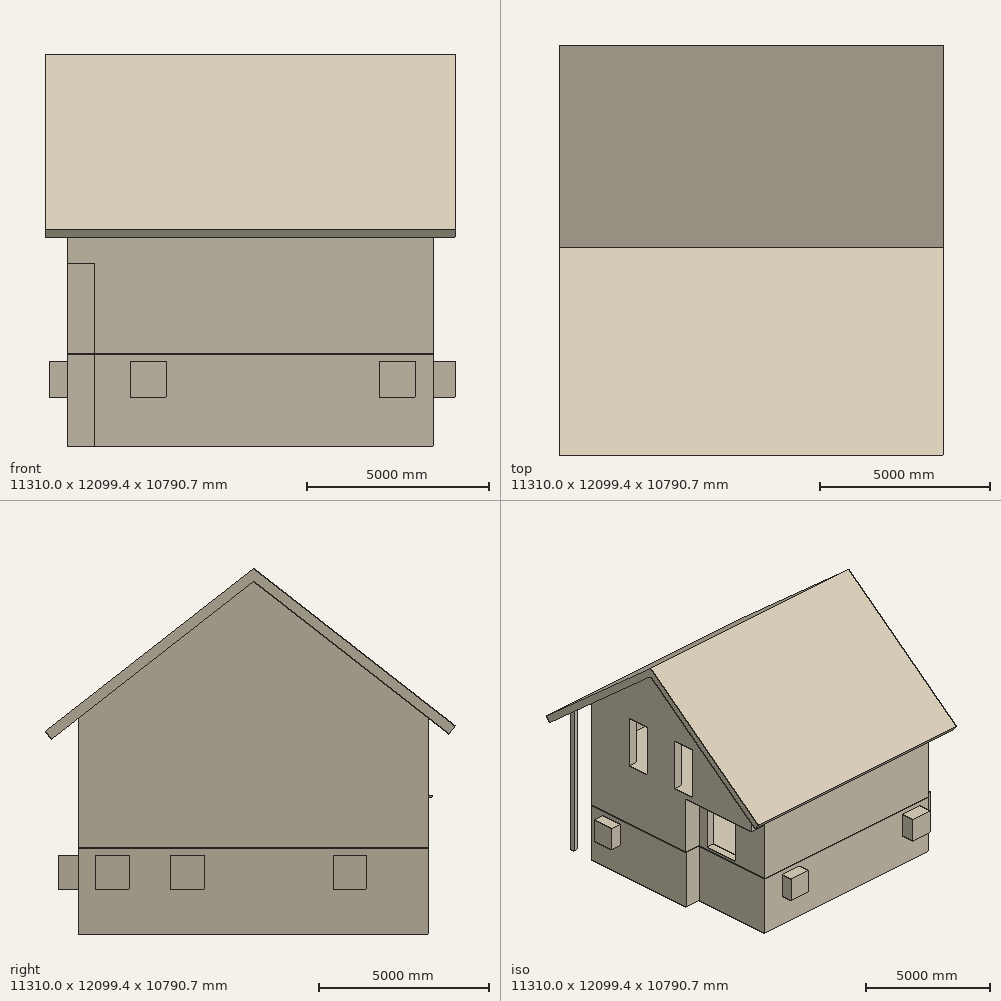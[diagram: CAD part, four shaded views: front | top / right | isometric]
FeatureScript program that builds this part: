
annotation { "Feature Type Name" : "Feature", "Feature Type Description" : "" }
export const myFeature = defineFeature(function(context is Context, id is Id, definition is map)
    precondition{}
    {
        {
            var Q0;
            Q0=qCreatedBy(makeId("Top.planeOp"),FACE);
            var sketch = newSketch(context, id + "F0", { "sketchPlane" : qUnion([Q0])});
            skLineSegment(sketch, "E0", {"start": v(0, 3573.84) * mm, "end": v(0, -3596.64) * mm, "construction": true});
            skLineSegment(sketch, "E1", {"start": v(-3920.01, 0) * mm, "end": v(4005.74, 0) * mm, "construction": true});
            skLineSegment(sketch, "E2.bottom", {"start": v(-435, 5165) * mm, "end": v(5055, 5165) * mm});
            skLineSegment(sketch, "E2.top", {"start": v(-4305, -5165) * mm, "end": v(5055, -5165) * mm});
            skLineSegment(sketch, "E2.left", {"start": v(-5055, 3965) * mm, "end": v(-5055, -1415) * mm});
            skLineSegment(sketch, "E2.right", {"start": v(5055, 5165) * mm, "end": v(5055, -5165) * mm});
            skPoint(sketch, "E2.middle", {"position": v(0, 0) * mm});
            skLineSegment(sketch, "E3", {"start": v(-5055, -1415) * mm, "end": v(-4305, -1415) * mm});
            skLineSegment(sketch, "E4", {"start": v(-4305, -1415) * mm, "end": v(-4305, -5165) * mm});
            skLineSegment(sketch, "E5", {"start": v(-435, 5165) * mm, "end": v(-435, 3965) * mm});
            skLineSegment(sketch, "E6", {"start": v(-435, 3965) * mm, "end": v(-5055, 3965) * mm});
            skLineSegment(sketch, "E7.bottom", {"start": v(-5055, 5165) * mm, "end": v(-4855, 5165) * mm});
            skLineSegment(sketch, "E7.top", {"start": v(-5055, 4965) * mm, "end": v(-4855, 4965) * mm});
            skLineSegment(sketch, "E7.left", {"start": v(-5055, 5165) * mm, "end": v(-5055, 4965) * mm});
            skLineSegment(sketch, "E7.right", {"start": v(-4855, 5165) * mm, "end": v(-4855, 4965) * mm});
            skSolve(sketch);
        }
        {
            var Q0;
            Q0=makeQuery(id+"F0.imprint","IMPRINT",FACE,{"disambiguationData":[TD([[makeQuery(id+"F0.imprint","IMPRINT",EDGE,{"derivedFrom":sQuery(id+"F0.wireOp",EDGE,"E2.bottom")}),-1.0]])]});
            var Q1;
            Q1=makeQuery(id+"F0.imprint","IMPRINT",FACE,{"disambiguationData":[TD([[makeQuery(id+"F0.imprint","IMPRINT",EDGE,{"derivedFrom":sQuery(id+"F0.wireOp",EDGE,"E7.bottom")}),-1.0]])]});
            extrude(context, id + "F1", {"entities" : qUnion([Q0, Q1]), "depth" : 7880 * mm});
        }
        {
            var Q0;
            Q0=makeQuery(id+"F0.imprint","IMPRINT",FACE,{"disambiguationData":[TD([[makeQuery(id+"F0.imprint","IMPRINT",EDGE,{"derivedFrom":sQuery(id+"F0.wireOp",EDGE,"E2.bottom")}),-1.0]])]});
            var Q1;
            Q1=makeQuery(id+"F0.imprint","IMPRINT",FACE,{"disambiguationData":[TD([[makeQuery(id+"F0.imprint","IMPRINT",EDGE,{"derivedFrom":sQuery(id+"F0.wireOp",EDGE,"E7.bottom")}),-1.0]])]});
            extrude(context, id + "F2", {"entities" : qUnion([Q0, Q1]), "operationType" : NewBodyOperationType.ADD, "oppositeDirection" : true, "depth" : 2530 * mm});
        }
        {
            var Q0;
            Q0=makeQuery(id+"F1.opExtrude","CAP_FACE",FACE,{"disambiguationData":[OSD([sQuery(id+"F0.wireOp",EDGE,"E2.bottom"),sQuery(id+"F0.wireOp",EDGE,"E2.top"),sQuery(id+"F0.wireOp",EDGE,"E2.left"),sQuery(id+"F0.wireOp",EDGE,"E2.right")])],"isStart":false});
            shell(context, id + "F3", {"entities" : qUnion([Q0]), "thickness" : 360 * mm});
        }
        {
            var Q0;
            {var subQ0=sQuery(id+"F0.wireOp",EDGE,"E2.right");Q0=makeQuery(id+"F2.boolean.opBoolean","MERGE",FACE,{"derivedFrom":[makeQuery(id+"F1.opExtrude","SWEPT_FACE",FACE,{"disambiguationData":[OSD([subQ0])]}),makeQuery(id+"F2.opExtrude","SWEPT_FACE",FACE,{"disambiguationData":[OSD([subQ0])]})]});}
            var sketch = newSketch(context, id + "F4", { "sketchPlane" : qUnion([Q0])});
            skLineSegment(sketch, "E8", {"start": v(0, 10151.05) * mm, "end": v(0, -3326.69) * mm, "construction": true});
            skPoint(sketch, "E9", {"position": v(0, 7880) * mm});
            skLineSegment(sketch, "E10", {"start": v(0, 7880) * mm, "end": v(5165, 3844.66) * mm});
            skLineSegment(sketch, "E11", {"start": v(0, 7880) * mm, "end": v(-5165, 3844.66) * mm});
            skLineSegment(sketch, "E12", {"start": v(5165, 3844.66) * mm, "end": v(5165, 7880) * mm});
            skLineSegment(sketch, "E13", {"start": v(5165, 7880) * mm, "end": v(0, 7880) * mm});
            skLineSegment(sketch, "E14", {"start": v(0, 7880) * mm, "end": v(-5165, 7880) * mm});
            skLineSegment(sketch, "E15", {"start": v(-5165, 7880) * mm, "end": v(-5165, 3844.66) * mm});
            skSolve(sketch);
        }
        {
            var Q0;
            Q0 = qSketchRegion(id + "F4", true);
            var Q1;
            {var subQ0=sQuery(id+"F0.wireOp",EDGE,"E2.left");Q1=makeQuery(id+"F2.boolean.opBoolean","MERGE",FACE,{"derivedFrom":[makeQuery(id+"F1.opExtrude","SWEPT_FACE",FACE,{"disambiguationData":[OSD([subQ0])]}),makeQuery(id+"F2.opExtrude","SWEPT_FACE",FACE,{"disambiguationData":[OSD([subQ0])]})]});}
            extrude(context, id + "F5", {"entities" : qUnion([Q0]), "operationType" : NewBodyOperationType.REMOVE, "endBound" : BoundingType.UP_TO_SURFACE, "oppositeDirection" : true, "endBoundEntityFace" : qUnion([Q1]), "depth" : 25 * mm});
        }
        {
            var Q0;
            Q0=qCreatedBy(makeId("Right.planeOp"),FACE);
            var sketch = newSketch(context, id + "F6", { "sketchPlane" : qUnion([Q0])});
            skLineSegment(sketch, "E16", {"start": v(0, 7880) * mm, "end": v(5765, 3375.89) * mm});
            skLineSegment(sketch, "E17", {"start": v(0, 7880) * mm, "end": v(-5965, 3219.63) * mm});
            skLineSegment(sketch, "E18.0", {"start": v(0, 8260.7) * mm, "end": v(-6149.7, 3456.03) * mm});
            skLineSegment(sketch, "E18.1", {"start": v(0, 8260.7) * mm, "end": v(5949.7, 3612.3) * mm});
            skLineSegment(sketch, "E19", {"start": v(5949.7, 3612.3) * mm, "end": v(5765, 3375.89) * mm});
            skLineSegment(sketch, "E20", {"start": v(-6149.7, 3456.03) * mm, "end": v(-5965, 3219.63) * mm});
            skSolve(sketch);
        }
        {
            var Q0;
            Q0 = qSketchRegion(id + "F6", true);
            extrude(context, id + "F7", {"entities" : qUnion([Q0]), "operationType" : NewBodyOperationType.ADD, "depth" : 5655 * mm, "hasSecondDirection" : true, "secondDirectionOppositeDirection" : true, "secondDirectionDepth" : 5655 * mm});
        }
        {
            var Q0;
            Q0=qCreatedBy(makeId("Top.planeOp"),FACE);
            cPlane(context, id + "F8", {"entities" : qUnion([Q0]), "cplaneType" : CPlaneType.OFFSET, "offset" : 2500 * mm, "width" : 150 * mm, "height" : 150 * mm});
        }
        {
            var Q0;
            Q0=qCreatedBy(id+"F8.planeOp",FACE);
            var sketch = newSketch(context, id + "F9", { "sketchPlane" : qUnion([Q0])});
            skLineSegment(sketch, "E21.bottom", {"start": v(-4305, -1415) * mm, "end": v(-5055, -1415) * mm});
            skLineSegment(sketch, "E21.top", {"start": v(-4305, -5165) * mm, "end": v(-5055, -5165) * mm});
            skLineSegment(sketch, "E21.left", {"start": v(-4305, -1415) * mm, "end": v(-4305, -5165) * mm});
            skLineSegment(sketch, "E21.right", {"start": v(-5055, -1415) * mm, "end": v(-5055, -5165) * mm});
            skSolve(sketch);
        }
        {
            var Q0;
            Q0 = qSketchRegion(id + "F9", true);
            extrude(context, id + "F10", {"entities" : qUnion([Q0]), "operationType" : NewBodyOperationType.ADD, "endBound" : BoundingType.UP_TO_NEXT, "depth" : 25 * mm});
        }
        {
            var Q0;
            Q0=qCreatedBy(makeId("Top.planeOp"),FACE);
            cPlane(context, id + "F11", {"entities" : qUnion([Q0]), "cplaneType" : CPlaneType.OFFSET, "offset" : 200 * mm, "oppositeDirection" : true, "width" : 150 * mm, "height" : 150 * mm});
        }
        {
            var Q0;
            Q0=qCreatedBy(id+"F11.planeOp",FACE);
            var sketch = newSketch(context, id + "F12", { "sketchPlane" : qUnion([Q0])});
            skLineSegment(sketch, "E22.bottom", {"start": v(-5055, 3335) * mm, "end": v(-5555, 3335) * mm});
            skLineSegment(sketch, "E22.top", {"start": v(-5055, 2335) * mm, "end": v(-5555, 2335) * mm});
            skLineSegment(sketch, "E22.left", {"start": v(-5055, 3335) * mm, "end": v(-5055, 2335) * mm});
            skLineSegment(sketch, "E22.right", {"start": v(-5555, 3335) * mm, "end": v(-5555, 2335) * mm});
            skLineSegment(sketch, "E23.bottom", {"start": v(5055, 3335) * mm, "end": v(5555, 3335) * mm});
            skLineSegment(sketch, "E23.top", {"start": v(5055, 2335) * mm, "end": v(5555, 2335) * mm});
            skLineSegment(sketch, "E23.left", {"start": v(5055, 3335) * mm, "end": v(5055, 2335) * mm});
            skLineSegment(sketch, "E23.right", {"start": v(5555, 3335) * mm, "end": v(5555, 2335) * mm});
            skLineSegment(sketch, "E24.bottom", {"start": v(5055, -1465) * mm, "end": v(5555, -1465) * mm});
            skLineSegment(sketch, "E24.top", {"start": v(5055, -2465) * mm, "end": v(5555, -2465) * mm});
            skLineSegment(sketch, "E24.left", {"start": v(5055, -1465) * mm, "end": v(5055, -2465) * mm});
            skLineSegment(sketch, "E24.right", {"start": v(5555, -1465) * mm, "end": v(5555, -2465) * mm});
            skLineSegment(sketch, "E25.bottom", {"start": v(5055, -3665) * mm, "end": v(5655, -3665) * mm});
            skLineSegment(sketch, "E25.top", {"start": v(5055, -4665) * mm, "end": v(5655, -4665) * mm});
            skLineSegment(sketch, "E25.left", {"start": v(5055, -3665) * mm, "end": v(5055, -4665) * mm});
            skLineSegment(sketch, "E25.right", {"start": v(5655, -3665) * mm, "end": v(5655, -4665) * mm});
            skLineSegment(sketch, "E26.bottom", {"start": v(4555, -5165) * mm, "end": v(3555, -5165) * mm});
            skLineSegment(sketch, "E26.top", {"start": v(4555, -5765) * mm, "end": v(3555, -5765) * mm});
            skLineSegment(sketch, "E26.left", {"start": v(4555, -5165) * mm, "end": v(4555, -5765) * mm});
            skLineSegment(sketch, "E26.right", {"start": v(3555, -5165) * mm, "end": v(3555, -5765) * mm});
            skLineSegment(sketch, "E27.bottom", {"start": v(-3305, -5165) * mm, "end": v(-2305, -5165) * mm});
            skLineSegment(sketch, "E27.top", {"start": v(-3305, -5665) * mm, "end": v(-2305, -5665) * mm});
            skLineSegment(sketch, "E27.left", {"start": v(-3305, -5165) * mm, "end": v(-3305, -5665) * mm});
            skLineSegment(sketch, "E27.right", {"start": v(-2305, -5165) * mm, "end": v(-2305, -5665) * mm});
            skSolve(sketch);
        }
        {
            var Q0;
            Q0 = qSketchRegion(id + "F12", true);
            extrude(context, id + "F13", {"entities" : qUnion([Q0]), "operationType" : NewBodyOperationType.ADD, "oppositeDirection" : true, "depth" : 1000 * mm});
        }
        {
            var Q0;
            {var subQ0=sQuery(id+"F0.wireOp",EDGE,"E4");Q0=makeQuery(id+"F2.boolean.opBoolean","MERGE",FACE,{"derivedFrom":[makeQuery(id+"F1.opExtrude","SWEPT_FACE",FACE,{"disambiguationData":[OSD([subQ0])]}),makeQuery(id+"F2.opExtrude","SWEPT_FACE",FACE,{"disambiguationData":[OSD([subQ0])]})]});}
            var sketch = newSketch(context, id + "F14", { "sketchPlane" : qUnion([Q0])});
            skLineSegment(sketch, "E28", {"start": v(-4224.63, 0) * mm, "end": v(4783.34, 0) * mm, "construction": true});
            skLineSegment(sketch, "E29.bottom", {"start": v(1869.6, 2250) * mm, "end": v(3469.6, 2250) * mm});
            skLineSegment(sketch, "E29.top", {"start": v(1869.6, 150) * mm, "end": v(3469.6, 150) * mm});
            skLineSegment(sketch, "E29.left", {"start": v(1869.6, 2250) * mm, "end": v(1869.6, 150) * mm});
            skLineSegment(sketch, "E29.right", {"start": v(3469.6, 2250) * mm, "end": v(3469.6, 150) * mm});
            skSolve(sketch);
        }
        {
            var Q0;
            Q0 = qSketchRegion(id + "F14", true);
            extrude(context, id + "F15", {"entities" : qUnion([Q0]), "operationType" : NewBodyOperationType.REMOVE, "endBound" : BoundingType.UP_TO_NEXT, "oppositeDirection" : true, "depth" : 25 * mm});
        }
        {
            var Q0;
            Q0=qCreatedBy(makeId("Top.planeOp"),FACE);
            var sketch = newSketch(context, id + "F16", { "sketchPlane" : qUnion([Q0])});
            skLineSegment(sketch, "E30", {"start": v(-5055, 3965) * mm, "end": v(-434.34, 3965) * mm});
            skLineSegment(sketch, "E31", {"start": v(-434.34, 3965) * mm, "end": v(-434.34, 5165) * mm});
            skLineSegment(sketch, "E32", {"start": v(-434.34, 5165) * mm, "end": v(5055, 5165) * mm});
            skLineSegment(sketch, "E33", {"start": v(5055, 5165) * mm, "end": v(5055, -5165) * mm});
            skLineSegment(sketch, "E34", {"start": v(5055, -5165) * mm, "end": v(-4305, -5165) * mm});
            skLineSegment(sketch, "E35", {"start": v(-4305, -5165) * mm, "end": v(-4305, -1415) * mm});
            skLineSegment(sketch, "E36", {"start": v(-4305, -1415) * mm, "end": v(-5055, -1415) * mm});
            skLineSegment(sketch, "E37", {"start": v(-5055, -1415) * mm, "end": v(-5055, 3965) * mm});
            skLineSegment(sketch, "E38.0", {"start": v(-5045, -1405) * mm, "end": v(-5045, 3955) * mm});
            skLineSegment(sketch, "E38.1", {"start": v(-4295, -1405) * mm, "end": v(-5045, -1405) * mm});
            skLineSegment(sketch, "E38.2", {"start": v(-5045, 3955) * mm, "end": v(-424.34, 3955) * mm});
            skLineSegment(sketch, "E38.3", {"start": v(-4295, -5155) * mm, "end": v(-4295, -1405) * mm});
            skLineSegment(sketch, "E38.4", {"start": v(-424.34, 3955) * mm, "end": v(-424.34, 5155) * mm});
            skLineSegment(sketch, "E38.5", {"start": v(-424.34, 5155) * mm, "end": v(5045, 5155) * mm});
            skLineSegment(sketch, "E38.6", {"start": v(5045, 5155) * mm, "end": v(5045, -5155) * mm});
            skLineSegment(sketch, "E38.7", {"start": v(5045, -5155) * mm, "end": v(-4295, -5155) * mm});
            skSolve(sketch);
        }
        {
            var Q0;
            Q0 = qSketchRegion(id + "F16", true);
            extrude(context, id + "F17", {"entities" : qUnion([Q0]), "operationType" : NewBodyOperationType.REMOVE, "depth" : 25 * mm});
        }
        {
            var Q0;
            {var subQ0=sQuery(id+"F0.wireOp",EDGE,"E2.bottom");Q0=makeQuery(id+"F2.boolean.opBoolean","MERGE",FACE,{"derivedFrom":[makeQuery(id+"F1.opExtrude","SWEPT_FACE",FACE,{"disambiguationData":[OSD([subQ0])]}),makeQuery(id+"F2.opExtrude","SWEPT_FACE",FACE,{"disambiguationData":[OSD([subQ0])]})]});}
            var sketch = newSketch(context, id + "F18", { "sketchPlane" : qUnion([Q0])});
            skCircle(sketch, "E39", {"center": v(-1365, 1530.35) * mm, "radius": 25 * mm});
            skSolve(sketch);
        }
        {
            var Q0;
            Q0 = qSketchRegion(id + "F18", true);
            extrude(context, id + "F19", {"entities" : qUnion([Q0]), "operationType" : NewBodyOperationType.ADD, "depth" : 100 * mm});
        }
        {
            var Q0;
            {var subQ3=sQuery(id+"F0.wireOp",EDGE,"E2.top");var subQ4=sQuery(id+"F9.wireOp",EDGE,"E21.right");var subQ5=sQuery(id+"F0.wireOp",EDGE,"E2.left");Q0=makeQuery(id+"F17.boolean.opBoolean","SPLIT",FACE,{"disambiguationData":[TD([makeQuery(id+"F1.opExtrude","SWEPT_FACE",FACE,{"disambiguationData":[OSD([subQ3])]})])],"derivedFrom":makeQuery(id+"F10.boolean.opBoolean","MERGE",FACE,{"derivedFrom":[makeQuery(id+"F2.boolean.opBoolean","MERGE",FACE,{"derivedFrom":[makeQuery(id+"F1.opExtrude","SWEPT_FACE",FACE,{"disambiguationData":[OSD([subQ5])]}),makeQuery(id+"F2.opExtrude","SWEPT_FACE",FACE,{"disambiguationData":[OSD([subQ5])]})]}),makeQuery(id+"F10.opExtrude","SWEPT_FACE",FACE,{"disambiguationData":[OSD([subQ4])]})]})});}
            var sketch = newSketch(context, id + "F20", { "sketchPlane" : qUnion([Q0])});
            skLineSegment(sketch, "E40.bottom", {"start": v(5165, 2500) * mm, "end": v(-3965, 2500) * mm});
            skLineSegment(sketch, "E40.top", {"start": v(5165, 2740) * mm, "end": v(-3965, 2740) * mm});
            skLineSegment(sketch, "E40.left", {"start": v(5165, 2500) * mm, "end": v(5165, 2740) * mm});
            skLineSegment(sketch, "E40.right", {"start": v(-3965, 2500) * mm, "end": v(-3965, 2740) * mm});
            skLineSegment(sketch, "E41", {"start": v(-2751.87, 5730) * mm, "end": v(2751.87, 5730) * mm});
            skLineSegment(sketch, "E42", {"start": v(2751.87, 5730) * mm, "end": v(3059.06, 5490) * mm});
            skLineSegment(sketch, "E43", {"start": v(3059.06, 5490) * mm, "end": v(-3059.06, 5490) * mm});
            skLineSegment(sketch, "E44", {"start": v(-3059.06, 5490) * mm, "end": v(-2751.87, 5730) * mm});
            skSolve(sketch);
        }
        {
            var Q0;
            Q0 = qSketchRegion(id + "F20", true);
            var Q1;
            {var subQ2=sQuery(id+"F0.wireOp",EDGE,"E2.right");Q1=makeQuery(id+"F17.boolean.opBoolean","SPLIT",FACE,{"disambiguationData":[TD([makeQuery(id+"F7.opExtrude","SWEPT_FACE",FACE,{"disambiguationData":[OSD([sQuery(id+"F6.wireOp",EDGE,"E16")])]})])],"derivedFrom":makeQuery(id+"F2.boolean.opBoolean","MERGE",FACE,{"derivedFrom":[makeQuery(id+"F1.opExtrude","SWEPT_FACE",FACE,{"disambiguationData":[OSD([subQ2])]}),makeQuery(id+"F2.opExtrude","SWEPT_FACE",FACE,{"disambiguationData":[OSD([subQ2])]})]})});}
            extrude(context, id + "F21", {"entities" : qUnion([Q0]), "operationType" : NewBodyOperationType.ADD, "endBound" : BoundingType.UP_TO_SURFACE, "oppositeDirection" : true, "endBoundEntityFace" : qUnion([Q1]), "depth" : 25 * mm});
        }
        {
            var Q0;
            {var subQ3=sQuery(id+"F0.wireOp",EDGE,"E2.top");var subQ4=sQuery(id+"F9.wireOp",EDGE,"E21.right");var subQ5=sQuery(id+"F0.wireOp",EDGE,"E2.left");Q0=makeQuery(id+"F17.boolean.opBoolean","SPLIT",FACE,{"disambiguationData":[TD([makeQuery(id+"F1.opExtrude","SWEPT_FACE",FACE,{"disambiguationData":[OSD([subQ3])]})])],"derivedFrom":makeQuery(id+"F10.boolean.opBoolean","MERGE",FACE,{"derivedFrom":[makeQuery(id+"F2.boolean.opBoolean","MERGE",FACE,{"derivedFrom":[makeQuery(id+"F1.opExtrude","SWEPT_FACE",FACE,{"disambiguationData":[OSD([subQ5])]}),makeQuery(id+"F2.opExtrude","SWEPT_FACE",FACE,{"disambiguationData":[OSD([subQ5])]})]}),makeQuery(id+"F10.opExtrude","SWEPT_FACE",FACE,{"disambiguationData":[OSD([subQ4])]})]})});}
            var sketch = newSketch(context, id + "F22", { "sketchPlane" : qUnion([Q0])});
            skLineSegment(sketch, "E45.bottom", {"start": v(-1792.5, 2740) * mm, "end": v(-782.5, 2740) * mm});
            skLineSegment(sketch, "E45.top", {"start": v(-1792.5, 4940) * mm, "end": v(-782.5, 4940) * mm});
            skLineSegment(sketch, "E45.left", {"start": v(-1792.5, 2740) * mm, "end": v(-1792.5, 4940) * mm});
            skLineSegment(sketch, "E45.right", {"start": v(-782.5, 2740) * mm, "end": v(-782.5, 4940) * mm});
            skLineSegment(sketch, "E46.bottom", {"start": v(782.5, 2740) * mm, "end": v(1792.5, 2740) * mm});
            skLineSegment(sketch, "E46.top", {"start": v(782.5, 4940) * mm, "end": v(1792.5, 4940) * mm});
            skLineSegment(sketch, "E46.left", {"start": v(782.5, 2740) * mm, "end": v(782.5, 4940) * mm});
            skLineSegment(sketch, "E46.right", {"start": v(1792.5, 2740) * mm, "end": v(1792.5, 4940) * mm});
            skLineSegment(sketch, "E47", {"start": v(0, 7880) * mm, "end": v(0, -2730.17) * mm, "construction": true});
            skSolve(sketch);
        }
        {
            var Q0;
            Q0 = qSketchRegion(id + "F22", true);
            extrude(context, id + "F23", {"entities" : qUnion([Q0]), "operationType" : NewBodyOperationType.REMOVE, "endBound" : BoundingType.UP_TO_NEXT, "oppositeDirection" : true, "depth" : 25 * mm});
        }
    });
